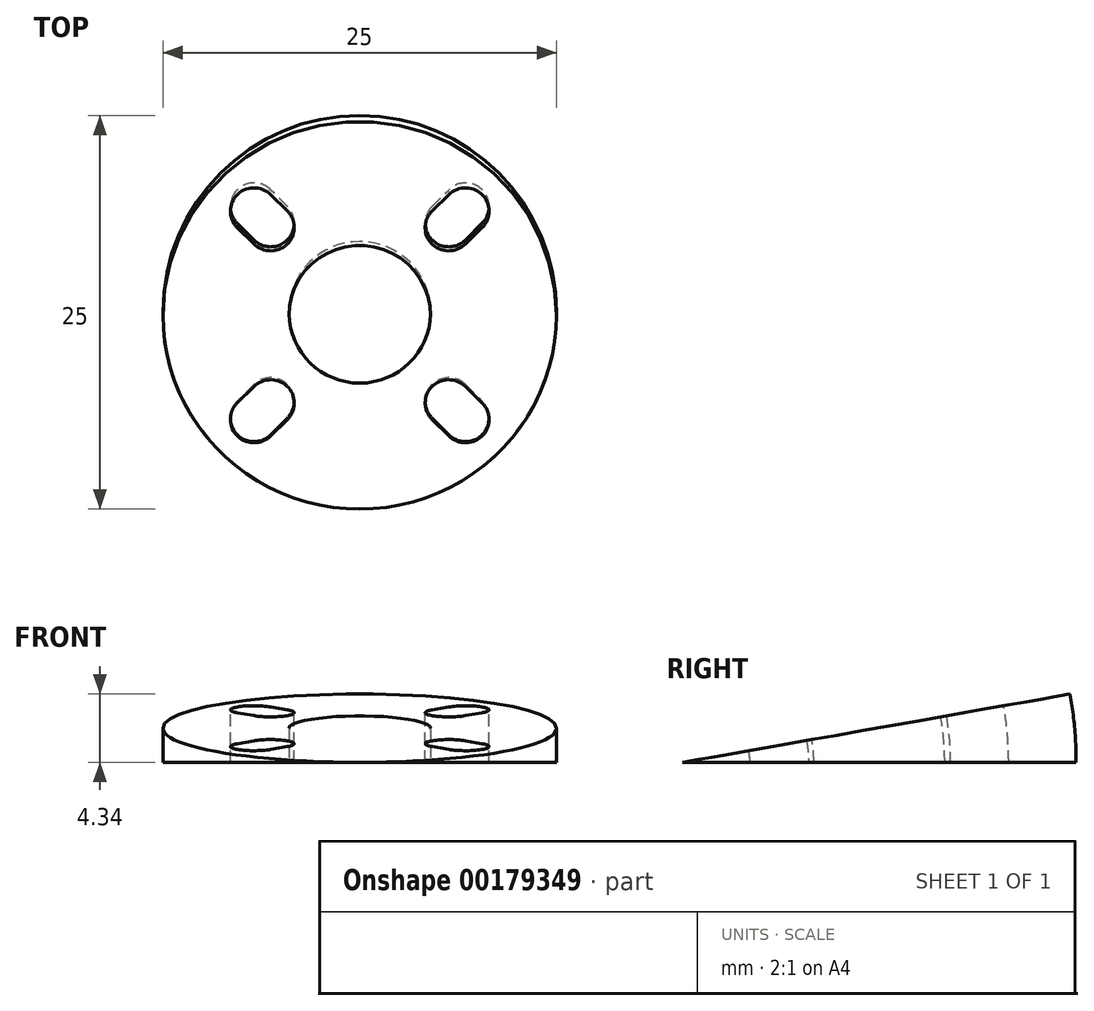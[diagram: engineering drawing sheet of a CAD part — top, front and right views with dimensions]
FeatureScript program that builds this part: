
annotation { "Feature Type Name" : "Feature", "Feature Type Description" : "" }
export const myFeature = defineFeature(function(context is Context, id is Id, definition is map)
    precondition{}
    {
        {
            var Q0;
            Q0=qCreatedBy(makeId("Top.planeOp"),FACE);
            var sketch = newSketch(context, id + "F0", { "sketchPlane" : qUnion([Q0])});
            skCircle(sketch, "E0", {"center": v(0, 0) * mm, "radius": 12.5 * mm});
            skLineSegment(sketch, "E1", {"start": v(0, -12.5) * mm, "end": v(45.94, -12.5) * mm, "construction": true});
            skCircle(sketch, "E2", {"center": v(0, 0) * mm, "radius": 4.5 * mm});
            skLineSegment(sketch, "E3", {"start": v(0, 0) * mm, "end": v(6.72, 6.72) * mm, "construction": true});
            skArc(sketch, "E4", {"start": v(4.6, 6.72) * mm, "mid": v(4.6, 4.6) * mm, "end": v(6.72, 4.6) * mm});
            skLineSegment(sketch, "E5", {"start": v(4.6, 6.72) * mm, "end": v(5.66, 7.78) * mm});
            skLineSegment(sketch, "E6", {"start": v(6.72, 4.6) * mm, "end": v(7.78, 5.66) * mm});
            skArc(sketch, "E7.trimOffspring", {"start": v(7.78, 5.66) * mm, "mid": v(7.78, 7.78) * mm, "end": v(5.66, 7.78) * mm});
            skArc(sketch, "E8.1.0", {"start": v(5.66, -7.78) * mm, "mid": v(7.78, -7.78) * mm, "end": v(7.78, -5.66) * mm});
            skLineSegment(sketch, "E8.1.1", {"start": v(6.72, -4.6) * mm, "end": v(7.78, -5.66) * mm});
            skArc(sketch, "E8.1.2", {"start": v(6.72, -4.6) * mm, "mid": v(4.6, -4.6) * mm, "end": v(4.6, -6.72) * mm});
            skLineSegment(sketch, "E8.1.3", {"start": v(4.6, -6.72) * mm, "end": v(5.66, -7.78) * mm});
            skArc(sketch, "E8.2.0", {"start": v(-7.78, -5.66) * mm, "mid": v(-7.78, -7.78) * mm, "end": v(-5.66, -7.78) * mm});
            skLineSegment(sketch, "E8.2.1", {"start": v(-4.6, -6.72) * mm, "end": v(-5.66, -7.78) * mm});
            skArc(sketch, "E8.2.2", {"start": v(-4.6, -6.72) * mm, "mid": v(-4.6, -4.6) * mm, "end": v(-6.72, -4.6) * mm});
            skLineSegment(sketch, "E8.2.3", {"start": v(-6.72, -4.6) * mm, "end": v(-7.78, -5.66) * mm});
            skArc(sketch, "E8.3.0", {"start": v(-5.66, 7.78) * mm, "mid": v(-7.78, 7.78) * mm, "end": v(-7.78, 5.66) * mm});
            skLineSegment(sketch, "E8.3.1", {"start": v(-6.72, 4.6) * mm, "end": v(-7.78, 5.66) * mm});
            skArc(sketch, "E8.3.2", {"start": v(-6.72, 4.6) * mm, "mid": v(-4.6, 4.6) * mm, "end": v(-4.6, 6.72) * mm});
            skLineSegment(sketch, "E8.3.3", {"start": v(-4.6, 6.72) * mm, "end": v(-5.66, 7.78) * mm});
            skLineSegment(sketch, "E8.anchor1", {"start": v(0, 0) * mm, "end": v(7.78, 5.66) * mm, "construction": true});
            skLineSegment(sketch, "E8.anchor2", {"start": v(0, 0) * mm, "end": v(-5.66, 7.78) * mm, "construction": true});
            skSolve(sketch);
        }
        {
            var Q0;
            Q0=makeQuery(id+"F0.imprint","IMPRINT",FACE,{"disambiguationData":[TD([[makeQuery(id+"F0.imprint","IMPRINT",EDGE,{"derivedFrom":sQuery(id+"F0.wireOp",EDGE,"E0")}),1.0]])]});
            var Q1;
            Q1=sQuery(id+"F0.wireOp",EDGE,"E1");
            revolve(context, id + "F1", {"entities" : qUnion([Q0]), "axis" : qUnion([Q1]), "revolveType" : RevolveType.ONE_DIRECTION, "angle" : 10 * degree});
        }
    });
